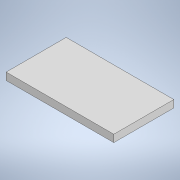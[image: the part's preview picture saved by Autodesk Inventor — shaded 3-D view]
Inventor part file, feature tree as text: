
AUTODESK INVENTOR PART (.ipt)
format: ipt  version: 2020.3 (Build 243373000, 373)  size: 89,600 bytes
history: native  units: mm
features: extrude x1, sketch x1
ambient origin geometry x8: Origin, YZ Plane, XZ Plane, XY Plane, X Axis, Y Axis, Z Axis, Center Point
bodies: Solid1 (feature_tree)
feature tree (2):
  extrude  "Extrusion1"  Depth=251.0mm
  sketch  "Sketch1"  dims[d0=140.0mm d1=251.0mm d2=17.0mm d3=0.0mm]
